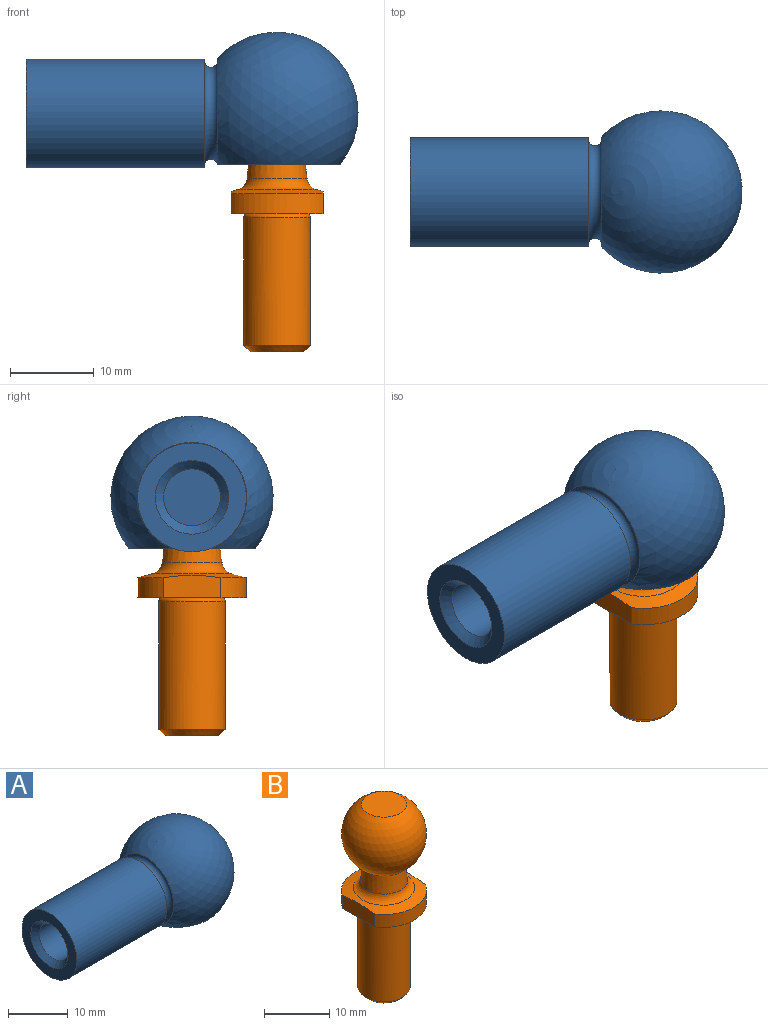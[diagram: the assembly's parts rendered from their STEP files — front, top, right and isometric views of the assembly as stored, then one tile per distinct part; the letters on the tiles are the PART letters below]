
ASSEMBLY  parts=2 mates=1
PART A: 15 faces, bbox 40x19.7x19.7 mm
  f0: cone r=3.9mm half-angle=45deg, axis (-1,0,0), area 34.7mm2, adj f1,f2
  f1: plane 13x13mm, normal (-1,0,0), area 71.9mm2, adj f0,f13
  f2: cylinder r=3.4mm len=13mm, axis (-1,0,0), area 277.7mm2, adj f0,f14
  f3: cylinder r=8.05mm len=16.1mm, axis (0,0,-1), area 91mm2, adj f4,f5
  f4: plane 16.1x16.1mm, normal (0,0,1), area 70.9mm2, adj f3,f6
  f5: plane 16.1x16.1mm, normal (0,0,-1), area 70.9mm2, adj f3,f7
  f6: cylinder r=6.5mm len=13mm, axis (0,0,1), area 122.5mm2, adj f4,f8
  f7: cylinder r=6.5mm len=13mm, axis (0,0,1), area 89.8mm2, adj f5,f9
  f8: plane 15.36x14.96mm, normal (0,0,-1), area 44.5mm2, adj f6,f10,f11
  f9: plane 13x13mm, normal (0,0,-1), area 0mm2, adj f7,f12
  f10: torus R=6.3mm, axis (-1,0,0), area 109.2mm2, adj f8,f11,f13
  f11: sphere r=9.7mm, area 809.2mm2, adj f8,f10
  f12: sphere r=6.5mm, area 269.5mm2, adj f9
  f13: cylinder r=6.5mm len=21.33mm, axis (-1,0,0), area 870.9mm2, adj f1,f10
  f14: plane 6.8x6.8mm, normal (-1,0,0), area 36.3mm2, adj f2
PART B: 14 faces, bbox 13.5x13.5x36 mm
  f0: cylinder r=4mm len=15.2mm, axis (0,0,-1), area 382mm2, adj f1,f2
  f1: cone r=4mm half-angle=45deg, axis (0,0,1), area 25.6mm2, adj f0,f3
  f2: torus R=3.5mm, axis (0,0,1), area 18.8mm2, adj f0,f4
  f3: plane 6.4x6.4mm, normal (0,0,-1), area 32.2mm2, adj f1
  f4: plane 13x11mm, normal (0,0,-1), area 84.9mm2, adj f2,f5,f6,f7,f8
  f5: cylinder r=6.5mm len=11mm, axis (0,0,-1), area 31.5mm2, adj f4,f6,f7,f9
  f6: plane 7.47x3.21mm, normal (1,0,0), area 17.8mm2, adj f4,f5,f8,f9
  f7: plane 7.47x3.21mm, normal (-1,0,0), area 17.8mm2, adj f4,f5,f8,f9
  f8: cylinder r=6.5mm len=11mm, axis (0,0,-1), area 31.5mm2, adj f4,f6,f7,f9
  f9: cone r=6.5mm half-angle=75deg, axis (0,0,-1), area 58.7mm2, adj f5,f6,f7,f8,f10
  f10: torus R=5.08mm, axis (0,0,-1), area 45.5mm2, adj f9,f11
  f11: cone r=3.59mm half-angle=6deg, axis (0,0,-1), area 69mm2, adj f10,f12
  f12: sphere r=6.5mm, area 454.7mm2, adj f11,f13
  f13: plane 7.1x7.1mm, normal (0,0,1), area 37.7mm2, adj f12
PLACE A t=(-15.82,16.74,26.19)mm fixed
PLACE B t=(-15.82,16.74,26.19)mm
MATE ball B.f11 <-> A.f3  axis (0,0,1) through (14.18,16.74,27.19)mm
